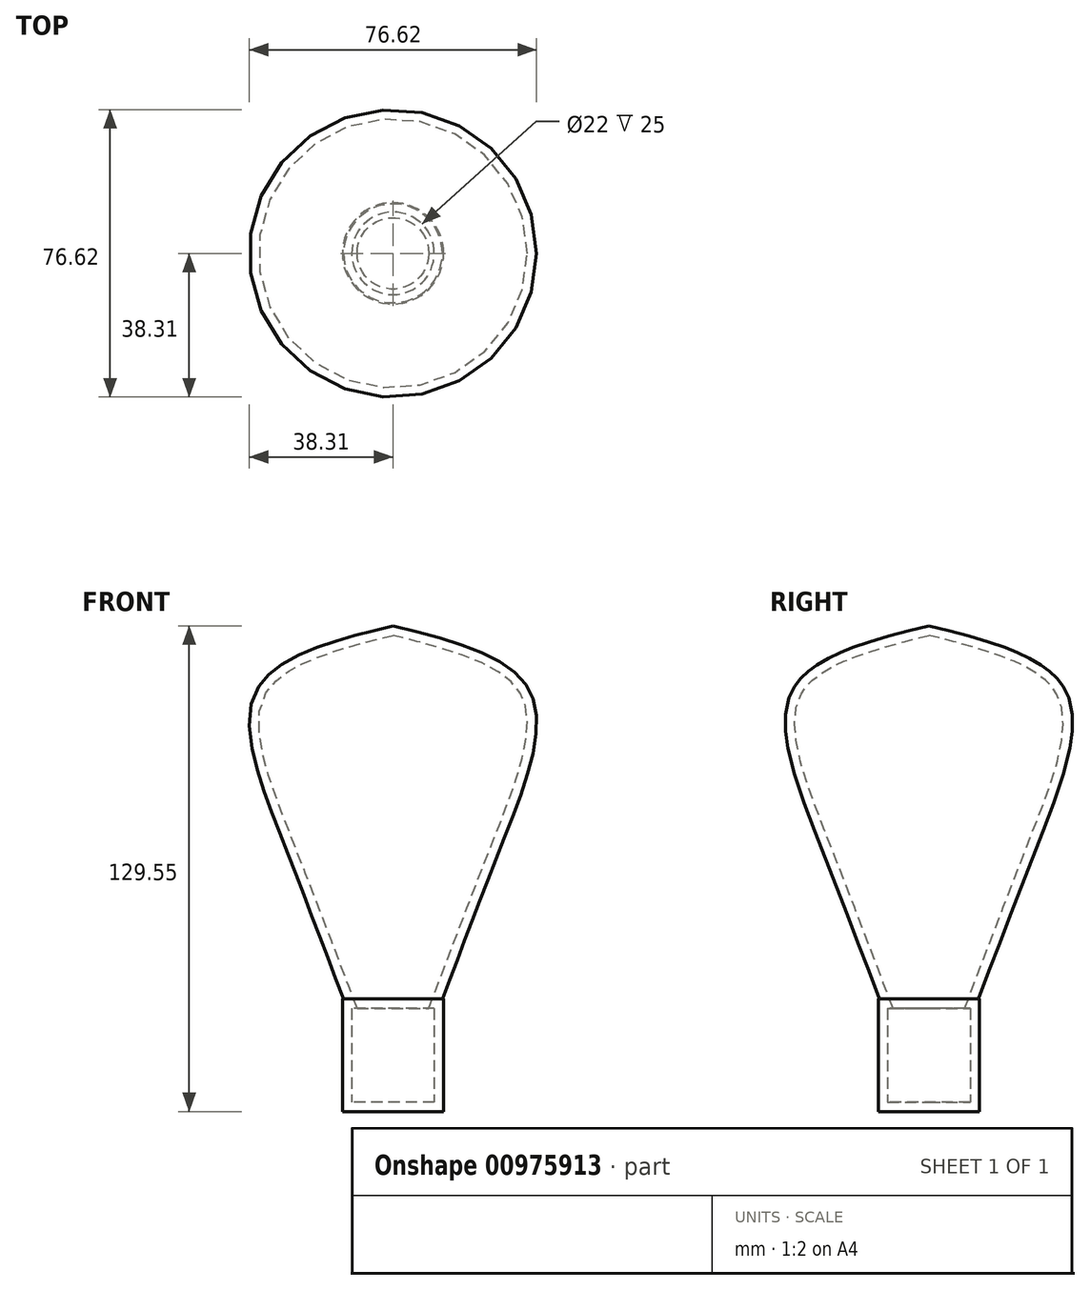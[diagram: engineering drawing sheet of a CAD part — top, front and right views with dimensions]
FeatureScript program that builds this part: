
annotation { "Feature Type Name" : "Feature", "Feature Type Description" : "" }
export const myFeature = defineFeature(function(context is Context, id is Id, definition is map)
    precondition{}
    {
        {
            var Q0;
            Q0=qCreatedBy(makeId("Top.planeOp"),FACE);
            var sketch = newSketch(context, id + "F0", { "sketchPlane" : qUnion([Q0])});
            skCircle(sketch, "E0", {"center": v(0, 0) * mm, "radius": 13.5 * mm});
            skSolve(sketch);
        }
        {
            var Q0;
            Q0 = qSketchRegion(id + "F0", true);
            extrude(context, id + "F1", {"entities" : qUnion([Q0]), "depth" : 30 * mm, "offsetDistance" : 25 * mm});
        }
        {
            var Q0;
            Q0=qCreatedBy(makeId("Front.planeOp"),FACE);
            var sketch = newSketch(context, id + "F2", { "sketchPlane" : qUnion([Q0])});
            skLineSegment(sketch, "E1", {"start": v(0, 29.55) * mm, "end": v(0, 129.55) * mm});
            skFitSpline(sketch, "E2", {"points": [v(13.1, 29.8) * mm, v(29.63, 72.81) * mm, v(36.64, 111.84) * mm, v(0, 129.55) * mm], "startDerivative": vector(45.36, 119.51) * mm, "endDerivative": vector(-145.86, 36.39) * mm});
            skLineSegment(sketch, "E3", {"start": v(0, 29.55) * mm, "end": v(13.1, 29.8) * mm});
            skSolve(sketch);
        }
        {
            var Q0;
            Q0=makeQuery(id+"F2.imprint","IMPRINT",FACE,{"disambiguationData":[TD([[makeQuery(id+"F2.imprint","IMPRINT",EDGE,{"derivedFrom":sQuery(id+"F2.wireOp",EDGE,"E1")}),-1.0]])]});
            var Q1;
            Q1=sQuery(id+"F2.wireOp",EDGE,"E1");
            revolve(context, id + "F3", {"operationType" : NewBodyOperationType.ADD, "surfaceOperationType" : NewSurfaceOperationType.NEW, "entities" : qUnion([Q0]), "axis" : qUnion([Q1]), "revolveType" : RevolveType.FULL});
        }
        {
            var Q0;
            Q0=makeQuery(id+"F3.opRevolve","SWEPT_FACE",FACE,{"disambiguationData":[OSD([sQuery(id+"F2.wireOp",EDGE,"E2")])]});
            var Q1;
            Q1=makeQuery(id+"F1.opExtrude","SWEPT_BODY",BODY,{"disambiguationData":[OSD([sQuery(id+"F0.wireOp",EDGE,"E0")])]});
            shell(context, id + "F4", {"isHollow" : true, "entities" : qUnion([Q0]), "parts" : qUnion([Q1]), "thickness" : 2.5 * mm});
        }
    });
